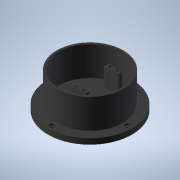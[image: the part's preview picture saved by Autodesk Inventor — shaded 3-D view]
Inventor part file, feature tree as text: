
AUTODESK INVENTOR PART (.ipt)
format: ipt  version: 2022 (Build 260153000, 153)  size: 329,728 bytes
history: native  units: in
note: dims shown in document units (in); Inventor stores cm internally (conversion verified against a paired STEP export)
features: extrude x17, sketch x17, thread x4
ambient origin geometry x8: Origin, YZ Plane, XZ Plane, XY Plane, X Axis, Y Axis, Z Axis, Center Point
bodies: Solid1 (feature_tree)
feature tree (38):
  extrude  "Extrusion1"  Depth=0.315in TaperAngle=0.0deg
  extrude  "Extrusion2"  Depth=0.1969in
  extrude  "Extrusion3"  Depth=0.1969in
  extrude  "Extrusion4"  Depth=0.1969in
  extrude  "Extrusion5"  Depth=0.1969in
  extrude  "Extrusion6"  Depth=0.315in
  extrude  "Extrusion7"  Depth=0.1969in
  extrude  "Extrusion8"  Depth=0.1969in
  extrude  "Extrusion9"  Depth=0.1181in TaperAngle=0.0deg
  extrude  "Extrusion10"  Depth=3.5433in
  extrude  "Extrusion11"  Depth=0.3937in
  extrude  "Extrusion12"  Depth=0.7874in
  thread  "Thread1"  [1 undecoded]
  thread  "Thread2"  [1 undecoded]
  thread  "Thread3"  [1 undecoded]
  thread  "Thread4"  [1 undecoded]
  extrude  "Extrusion13"  Depth=1.5748in
  extrude  "Extrusion14"  Depth=0.315in
  extrude  "Extrusion15"  Depth=0.315in TaperAngle=0.0deg
  extrude  "Extrusion16"  Depth=0.1575in
  extrude  "Extrusion17"  Depth=1.6732in TaperAngle=0.0deg
  sketch  "Sketch1"  dims[d0=4.7244in d1=0.315in d2=0.0in]
  sketch  "Sketch2"  dims[d3=0.315in d4=0.1969in]
  sketch  "Sketch3"  dims[d5=0.315in d6=0.1969in]
  sketch  "Sketch4"  dims[d7=0.315in d8=0.1969in]
  sketch  "Sketch5"  dims[d9=0.315in d10=0.1969in]
  sketch  "Sketch6"  dims[d11=0.315in d12=0.0in d13=0.315in]
  sketch  "Sketch7"  dims[d14=0.315in d15=0.1969in]
  sketch  "Sketch8"  dims[d16=0.315in d17=0.1969in]
  sketch  "Sketch9"  dims[d18=0.315in d19=0.1181in d20=0.0in]
  sketch  "Sketch10"  dims[d21=3.7402in d22=3.5433in]
  sketch  "Sketch11"  dims[d23=0.3937in d24=0.3543in]
  sketch  "Sketch12"  dims[d25=0.3937in d26=0.2756in d27=0.3937in d28=0.0in d29=0.3937in d30=0.3543in d31=0.7874in]
  sketch  "Sketch13"  dims[d32=0.2756in d33=1.5748in]
  sketch  "Sketch14"  dims[d34=0.315in d35=0.315in]
  sketch  "Sketch16"  dims[d36=0.315in d37=1.1024in d38=0.0in]
  sketch  "Sketch17"  dims[d39=0.1575in d40=0.1575in]
  sketch  "Sketch18"  dims[d41=1.1024in d42=0.0in d43=0.8661in d44=0.0in d45=0.0787in d46=0.1969in d47=0.1969in d48=0.1575in d49=0.1575in d50=0.0787in d51=0.1575in d52=0.1575in d53=0.3937in d54=0.0in d55=1.1024in d56=0.0in d57=0.3937in d58=1.437in d59=0.6654in d60=0.3937in d61=0.2362in d62=0.2362in d63=0.2362in d64=0.2362in d65=0.3937in d66=0.0in d67=0.6575in d68=0.0in d69=0.1004in d70=0.1004in d71=0.1988in d72=0.1988in d73=0.1988in d74=0.1988in d75=0.1063in d76=0.1063in d77=0.1063in d78=0.1063in d79=0.3937in d80=0.0in d81=0.3937in d82=0.0in d83=0.3937in d84=0.0in d85=0.3937in d86=0.0in d87=0.3937in d88=0.0in d89=1.8622in d90=0.0in d91=1.6732in d92=0.0in d93=1.6732in d94=0.0in d95=0.315in d96=0.0in d97=3.7402in d98=3.5433in d99=1.6732in d100=0.0in]
note: 4 required parameter values undecoded (feature->parameter linkage not recoverable at this tier; creation-order binding heuristic only, values carry confidence <= 0.55)
